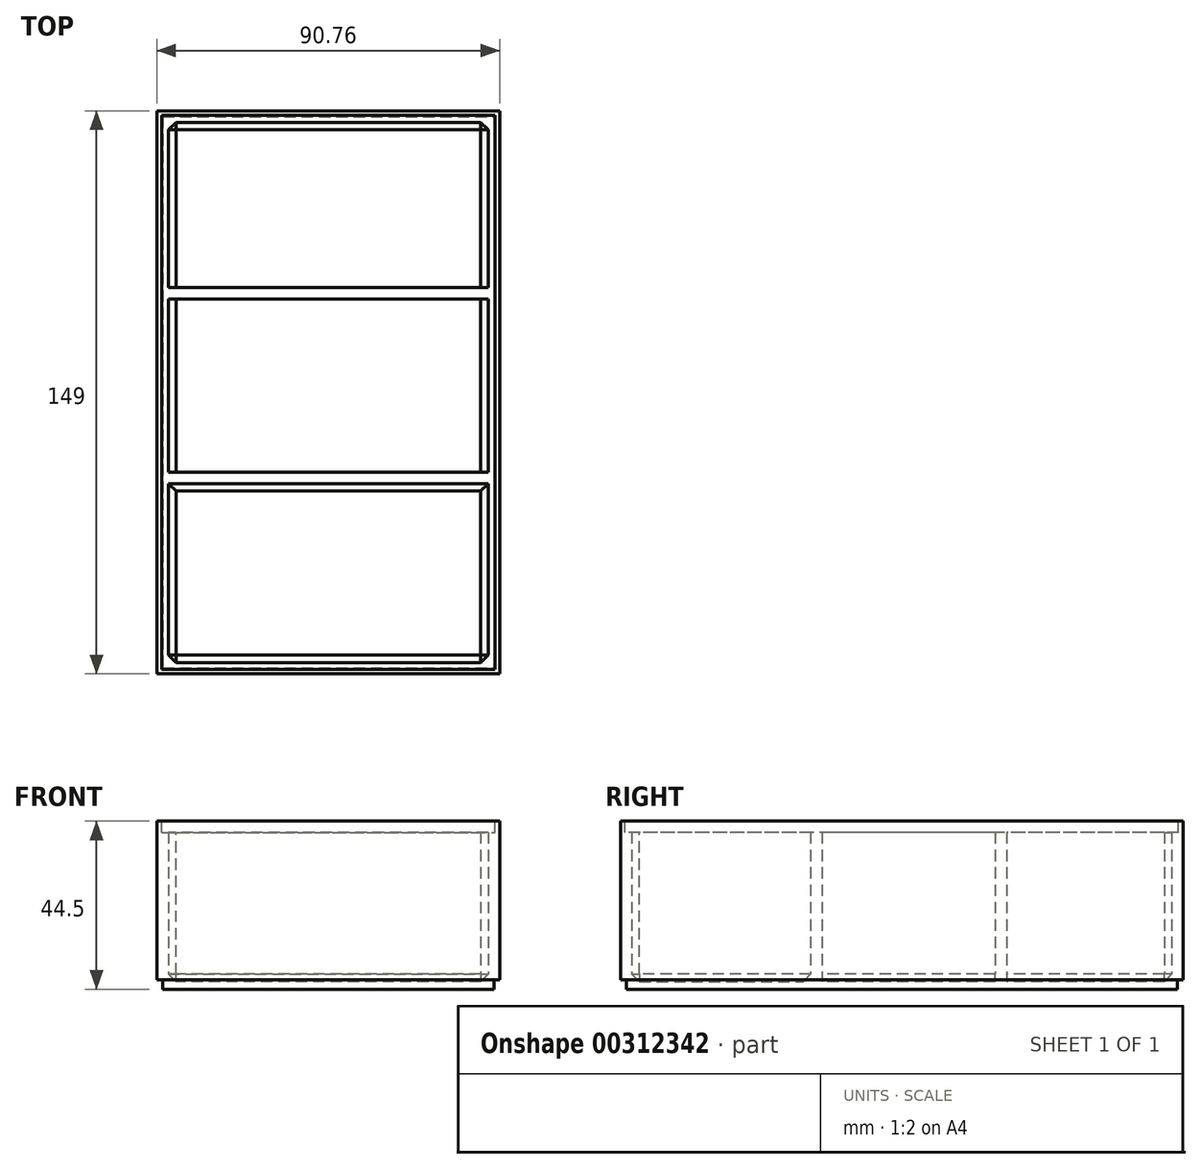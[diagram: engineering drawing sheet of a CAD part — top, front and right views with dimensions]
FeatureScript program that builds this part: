
annotation { "Feature Type Name" : "Feature", "Feature Type Description" : "" }
export const myFeature = defineFeature(function(context is Context, id is Id, definition is map)
    precondition{}
    {
        {
            assignVariable(context, id + "F0", {"name" : "BoxHeight", "anyValue" : 44.5});
        }
        {
            var Q0;
            Q0=qCreatedBy(makeId("Top.planeOp"),FACE);
            var sketch = newSketch(context, id + "F1", { "sketchPlane" : qUnion([Q0])});
            skLineSegment(sketch, "E0.bottom", {"start": v(-45.37, 74.5) * mm, "end": v(45.38, 74.5) * mm});
            skLineSegment(sketch, "E0.top", {"start": v(-45.38, -74.5) * mm, "end": v(45.37, -74.5) * mm});
            skLineSegment(sketch, "E0.left", {"start": v(-45.37, 74.5) * mm, "end": v(-45.38, -74.5) * mm});
            skLineSegment(sketch, "E0.right", {"start": v(45.38, 74.5) * mm, "end": v(45.37, -74.5) * mm});
            skPoint(sketch, "E0.middle", {"position": v(0, 0) * mm});
            skLineSegment(sketch, "E1.0", {"start": v(-42.37, 71.5) * mm, "end": v(42.38, 71.5) * mm});
            skLineSegment(sketch, "E1.1", {"start": v(-42.37, 71.5) * mm, "end": v(-42.38, -71.5) * mm});
            skLineSegment(sketch, "E1.2", {"start": v(-42.38, -71.5) * mm, "end": v(42.37, -71.5) * mm});
            skLineSegment(sketch, "E1.3", {"start": v(42.38, 71.5) * mm, "end": v(42.37, -71.5) * mm});
            skSolve(sketch);
        }
        {
            var Q0;
            Q0=makeQuery(id+"F1.imprint","IMPRINT",FACE,{"disambiguationData":[TD([[makeQuery(id+"F1.imprint","IMPRINT",EDGE,{"derivedFrom":sQuery(id+"F1.wireOp",EDGE,"E0.bottom")}),-1.0]])]});
            extrude(context, id + "F2", {"entities" : qUnion([Q0]), "depth" : (getVariable(context, 'BoxHeight')) * mm});
        }
        {
            var Q0;
            Q0=qSketchRegion(id+"F1",true);
            var Q1;
            Q1=makeQuery(id+"F1.imprint","IMPRINT",FACE,{"disambiguationData":[TD([[makeQuery(id+"F1.imprint","IMPRINT",EDGE,{"derivedFrom":sQuery(id+"F1.wireOp",EDGE,"E1.0")}),-1.0]])]});
            extrude(context, id + "F3", {"entities" : qUnion([Q0, Q1]), "operationType" : NewBodyOperationType.ADD, "depth" : 2 * mm});
        }
        {
            var Q0;
            Q0=makeQuery(id+"F2.opExtrude","CAP_FACE",FACE,{"disambiguationData":[OSD([sQuery(id+"F1.wireOp",EDGE,"E0.bottom"),sQuery(id+"F1.wireOp",EDGE,"E0.top"),sQuery(id+"F1.wireOp",EDGE,"E0.left"),sQuery(id+"F1.wireOp",EDGE,"E0.right"),sQuery(id+"F1.wireOp",EDGE,"E1.0"),sQuery(id+"F1.wireOp",EDGE,"E1.1"),sQuery(id+"F1.wireOp",EDGE,"E1.2"),sQuery(id+"F1.wireOp",EDGE,"E1.3")])],"isStart":false});
            var sketch = newSketch(context, id + "F4", { "sketchPlane" : qUnion([Q0])});
            skLineSegment(sketch, "E2.0", {"start": v(-45.37, 74.5) * mm, "end": v(45.38, 74.5) * mm});
            skLineSegment(sketch, "E2.1", {"start": v(45.38, 74.5) * mm, "end": v(45.37, -74.5) * mm});
            skLineSegment(sketch, "E2.2", {"start": v(-45.37, 74.5) * mm, "end": v(-45.38, -74.5) * mm});
            skLineSegment(sketch, "E2.3", {"start": v(-45.38, -74.5) * mm, "end": v(45.37, -74.5) * mm});
            skLineSegment(sketch, "E3.0", {"start": v(-44.17, 73.3) * mm, "end": v(-44.18, -73.3) * mm});
            skLineSegment(sketch, "E3.1", {"start": v(-44.17, 73.3) * mm, "end": v(44.17, 73.3) * mm});
            skLineSegment(sketch, "E3.2", {"start": v(44.18, 73.3) * mm, "end": v(44.17, -73.3) * mm});
            skLineSegment(sketch, "E3.3", {"start": v(-44.18, -73.3) * mm, "end": v(44.17, -73.3) * mm});
            skSolve(sketch);
        }
        {
            var Q0;
            Q0=makeQuery(id+"F4.imprint","IMPRINT",FACE,{"disambiguationData":[TD([[makeQuery(id+"F4.imprint","IMPRINT",EDGE,{"derivedFrom":sQuery(id+"F4.wireOp",EDGE,"E3.0")}),1.0]])]});
            extrude(context, id + "F5", {"entities" : qUnion([Q0]), "operationType" : NewBodyOperationType.REMOVE, "oppositeDirection" : true, "depth" : 3 * mm});
        }
        {
            var Q0;
            {var subQ0=sQuery(id+"F1.wireOp",EDGE,"E0.right");var subQ1=sQuery(id+"F1.wireOp",EDGE,"E0.left");var subQ2=sQuery(id+"F1.wireOp",EDGE,"E0.top");var subQ3=sQuery(id+"F1.wireOp",EDGE,"E0.bottom");Q0=makeQuery(id+"F3.boolean.opBoolean","MERGE",FACE,{"derivedFrom":[makeQuery(id+"F2.opExtrude","CAP_FACE",FACE,{"disambiguationData":[OSD([subQ3,subQ2,subQ1,subQ0,sQuery(id+"F1.wireOp",EDGE,"E1.0"),sQuery(id+"F1.wireOp",EDGE,"E1.1"),sQuery(id+"F1.wireOp",EDGE,"E1.2"),sQuery(id+"F1.wireOp",EDGE,"E1.3")])],"isStart":true}),makeQuery(id+"F3.opExtrude","CAP_FACE",FACE,{"disambiguationData":[OSD([subQ3,subQ2,subQ1,subQ0])],"isStart":true})]});}
            var sketch = newSketch(context, id + "F6", { "sketchPlane" : qUnion([Q0])});
            skLineSegment(sketch, "E4.0", {"start": v(-45.37, -74.5) * mm, "end": v(-45.38, 74.5) * mm});
            skLineSegment(sketch, "E5.0", {"start": v(-45.38, 74.5) * mm, "end": v(45.37, 74.5) * mm});
            skLineSegment(sketch, "E6.0", {"start": v(45.38, -74.5) * mm, "end": v(45.37, 74.5) * mm});
            skLineSegment(sketch, "E7.0", {"start": v(-45.37, -74.5) * mm, "end": v(45.38, -74.5) * mm});
            skLineSegment(sketch, "E8.0", {"start": v(-43.87, -73) * mm, "end": v(-43.88, 73) * mm});
            skLineSegment(sketch, "E8.1", {"start": v(-43.87, -73) * mm, "end": v(43.88, -73) * mm});
            skLineSegment(sketch, "E8.2", {"start": v(43.88, -73) * mm, "end": v(43.87, 73) * mm});
            skLineSegment(sketch, "E8.3", {"start": v(-43.88, 73) * mm, "end": v(43.87, 73) * mm});
            skSolve(sketch);
        }
        {
            var Q0;
            Q0=makeQuery(id+"F6.imprint","IMPRINT",FACE,{"disambiguationData":[TD([[makeQuery(id+"F6.imprint","IMPRINT",EDGE,{"derivedFrom":sQuery(id+"F6.wireOp",EDGE,"E4.0")}),-1.0]])]});
            extrude(context, id + "F7", {"entities" : qUnion([Q0]), "operationType" : NewBodyOperationType.REMOVE, "oppositeDirection" : true, "depth" : 2.5 * mm});
        }
        {
            var Q0;
            Q0=makeQuery(id+"F2.opExtrude","SWEPT_FACE",FACE,{"disambiguationData":[OSD([sQuery(id+"F1.wireOp",EDGE,"E1.3")])]});
            var sketch = newSketch(context, id + "F8", { "sketchPlane" : qUnion([Q0])});
            skLineSegment(sketch, "E9", {"start": v(71.5, 21.75) * mm, "end": v(22.63, 21.75) * mm, "construction": true});
            skPoint(sketch, "E9.endSnap0", {"position": v(71.5, 21.75) * mm});
            skLineSegment(sketch, "E10", {"start": v(22.63, 21.75) * mm, "end": v(-26.23, 21.75) * mm, "construction": true});
            skLineSegment(sketch, "E11", {"start": v(22.63, 41.5) * mm, "end": v(22.63, 2) * mm});
            skLineSegment(sketch, "E12", {"start": v(-26.23, 41.5) * mm, "end": v(-26.23, 2) * mm});
            skSolve(sketch);
        }
        {
            var Q0;
            Q0=sQuery(id+"F8.wireOp",EDGE,"E12");
            var Q1;
            Q1=sQuery(id+"F8.wireOp",EDGE,"E11");
            extrude(context, id + "F9", {"bodyType" : ToolBodyType.SURFACE, "surfaceEntities" : qUnion([Q0, Q1]), "endBound" : BoundingType.UP_TO_NEXT, "depth" : 25 * mm});
        }
        {
            var Q0;
            Q0=makeQuery(id+"F9.opExtrude","SWEPT_FACE",FACE,{"disambiguationData":[OSD([sQuery(id+"F8.wireOp",EDGE,"E12")])]});
            var Q1;
            Q1=makeQuery(id+"F9.opExtrude","SWEPT_FACE",FACE,{"disambiguationData":[OSD([sQuery(id+"F8.wireOp",EDGE,"E11")])]});
            extrude(context, id + "F10", {"entities" : qUnion([Q0, Q1]), "operationType" : NewBodyOperationType.ADD, "endBound" : BoundingType.SYMMETRIC, "depth" : 3 * mm});
        }
        {
            var Q0;
            Q0=makeQuery(id+"F3.boolean.opBoolean","INTERSECT",EDGE,{"derivedFrom":[makeQuery(id+"F2.opExtrude","SWEPT_FACE",FACE,{"disambiguationData":[OSD([sQuery(id+"F1.wireOp",EDGE,"E1.0")])]}),makeQuery(id+"F3.opExtrude","CAP_FACE",FACE,{"disambiguationData":[OSD([sQuery(id+"F1.wireOp",EDGE,"E0.bottom"),sQuery(id+"F1.wireOp",EDGE,"E0.top"),sQuery(id+"F1.wireOp",EDGE,"E0.left"),sQuery(id+"F1.wireOp",EDGE,"E0.right")])],"isStart":false})]});
            var Q1;
            Q1=makeQuery(id+"F3.boolean.opBoolean","INTERSECT",EDGE,{"derivedFrom":[makeQuery(id+"F2.opExtrude","SWEPT_FACE",FACE,{"disambiguationData":[OSD([sQuery(id+"F1.wireOp",EDGE,"E1.3")])]}),makeQuery(id+"F3.opExtrude","CAP_FACE",FACE,{"disambiguationData":[OSD([sQuery(id+"F1.wireOp",EDGE,"E0.bottom"),sQuery(id+"F1.wireOp",EDGE,"E0.top"),sQuery(id+"F1.wireOp",EDGE,"E0.left"),sQuery(id+"F1.wireOp",EDGE,"E0.right")])],"isStart":false})]});
            var Q2;
            Q2=makeQuery(id+"F3.boolean.opBoolean","INTERSECT",EDGE,{"derivedFrom":[makeQuery(id+"F2.opExtrude","SWEPT_FACE",FACE,{"disambiguationData":[OSD([sQuery(id+"F1.wireOp",EDGE,"E1.1")])]}),makeQuery(id+"F3.opExtrude","CAP_FACE",FACE,{"disambiguationData":[OSD([sQuery(id+"F1.wireOp",EDGE,"E0.bottom"),sQuery(id+"F1.wireOp",EDGE,"E0.top"),sQuery(id+"F1.wireOp",EDGE,"E0.left"),sQuery(id+"F1.wireOp",EDGE,"E0.right")])],"isStart":false})]});
            var Q3;
            Q3=makeQuery(id+"F3.boolean.opBoolean","INTERSECT",EDGE,{"derivedFrom":[makeQuery(id+"F2.opExtrude","SWEPT_FACE",FACE,{"disambiguationData":[OSD([sQuery(id+"F1.wireOp",EDGE,"E1.2")])]}),makeQuery(id+"F3.opExtrude","CAP_FACE",FACE,{"disambiguationData":[OSD([sQuery(id+"F1.wireOp",EDGE,"E0.bottom"),sQuery(id+"F1.wireOp",EDGE,"E0.top"),sQuery(id+"F1.wireOp",EDGE,"E0.left"),sQuery(id+"F1.wireOp",EDGE,"E0.right")])],"isStart":false})]});
            var Q4;
            Q4=makeQuery(id+"F2.opExtrude","SWEPT_EDGE",EDGE,{"disambiguationData":[OSD([sQuery(id+"F1.wireOp",EDGE,"E1.2"),sQuery(id+"F1.wireOp",EDGE,"E1.3")])]});
            var Q5;
            Q5=makeQuery(id+"F2.opExtrude","SWEPT_EDGE",EDGE,{"disambiguationData":[OSD([sQuery(id+"F1.wireOp",EDGE,"E1.0"),sQuery(id+"F1.wireOp",EDGE,"E1.3")])]});
            var Q6;
            Q6=makeQuery(id+"F2.opExtrude","SWEPT_EDGE",EDGE,{"disambiguationData":[OSD([sQuery(id+"F1.wireOp",EDGE,"E1.0"),sQuery(id+"F1.wireOp",EDGE,"E1.1")])]});
            var Q7;
            Q7=makeQuery(id+"F2.opExtrude","SWEPT_EDGE",EDGE,{"disambiguationData":[OSD([sQuery(id+"F1.wireOp",EDGE,"E1.1"),sQuery(id+"F1.wireOp",EDGE,"E1.2")])]});
            var Q8;
            Q8=makeQuery(id+"F10.opExtrude","CAP_EDGE",EDGE,{"disambiguationData":[OSD([sQuery(id+"F1.wireOp",EDGE,"E0.bottom"),sQuery(id+"F1.wireOp",EDGE,"E0.top"),sQuery(id+"F1.wireOp",EDGE,"E0.left"),sQuery(id+"F1.wireOp",EDGE,"E0.right")])],"isStart":false});
            var Q9;
            Q9=makeQuery(id+"F10.boolean.opBoolean","SPLIT",FACE,{"disambiguationData":[TD([makeQuery(id+"F2.opExtrude","SWEPT_FACE",FACE,{"disambiguationData":[OSD([sQuery(id+"F1.wireOp",EDGE,"E1.2")])]})])],"derivedFrom":makeQuery(id+"F3.opExtrude","CAP_FACE",FACE,{"disambiguationData":[OSD([sQuery(id+"F1.wireOp",EDGE,"E0.bottom"),sQuery(id+"F1.wireOp",EDGE,"E0.top"),sQuery(id+"F1.wireOp",EDGE,"E0.left"),sQuery(id+"F1.wireOp",EDGE,"E0.right")])],"isStart":false})});
            chamfer(context, id + "F11", {"entities" : qUnion([Q0, Q1, Q2, Q3, Q4, Q5, Q6, Q7, Q8, Q9]), "width" : 2 * mm, "tangentPropagation" : true});
        }
    });
